# Revit family: PRD_FrankeWS_HndDriers_DryersHandDryer_RODX310
name_source: partatom
category: Specialty Equipment
revit_build: Autodesk Revit 2018 (Build: 20190510_1515(x64)
units: mm (PartAtom-declared; Revit-internal decimal feet)

## family parameters
Cut with Voids When Loaded = No
Host = Face
OmniClass Number = 23.40.20.21.14
OmniClass Title = Hand and Hair Dryers
Part Type = Normal
Room Calculation Point = No
Round Connector Dimension = Use Diameter
Shared = No

## types (1)
- RODX310
    ApparentPower = 2200 VA
    AssetType = Fixed
    BIMObjectName = PRD_AR_HandDriers_DryersHandDryer_RODX310
    BodyEnclosure = Stainless steel
    BodyFinishAndColour = Stainless steel, satin finished
    BodyIngressProtectionMinimum = IPX1
    Category = Pr_40_70_62_37, Hand driers
    Color = Stainless steel
    Default Elevation = 1000 mm  [stored 3.28084 ft]
    Description = Touch free electronic warm air hand dryer for wall mounting, stainless steel, surface satin finished, material thickness 1.2 mm, infrared sensor activity for non-touch operation, sensor range adjustable from 10 to 30 cm, cable and plug not included.
    DurationUnit = year
    ElectricalDeviceNominalPower = 2200 VA
    ElectricalSupplyPowerRating = 2200 W
    ElectricalSupplyRatedOperationalVoltageUe = 230 V a.c.
    Features = Sensor range adjustable from 10 to 30 cm
    Finish = Satin finished
    Form = Touch free electronic warm air hand dryer for wall mounting
    GrossWeight = 7.58 kg
    HandDryerMaterial = PRD_AR_StainlessSteel_SatinFinished
    HasProtectiveEarth = Yes
    IP_Code = IPX1
    IfcExportAs = IfcElectricApplianceType
    IfcExportType = HANDDRYER
    InsulationStandardClass = NotKnown
    LoadClassification = Other
    Manufacturer = KWC Group AG
    ManufacturerName = KWC Group AG
    ManufacturerURL = www.kwc.com
    Material = Stainless steel
    Model = RODX310
    ModelNumber = 2000090055
    ModelReference = RODX310
    NBSDescription = Hand driers
    NBSReference = 45-35-72/334
    Name = DRYERS hand dryer RODX310
    NetWeight = 7.20 kg
    NoiseLevelAt1MMaximum = 68 dB
    NominalCurrent = 0 A
    NominalFrequencyRange = 50
    NominalHeight = 215 mm
    NominalLength = 314 mm  [stored 1.03018 ft]
    NominalVoltage = 230
    NominalWidth = 163 mm  [stored 0.534777 ft]
    NumberOfPoles = 1
    Operation = Automatic. No touch
    PhaseAngle = 0.00°
    PhaseReference = 0
    PowerFactor = 1
    ProductInformation = https://pim.kwc.com
    Size = 314 x 215 x 163 mm
    URL = www.kwc.com
    Uniclass2015Code = Pr_40_70_62_37
    Uniclass2015Title = Hand driers
    Uniclass2015Version = Products v1.5
    UsageCurrent = 0 A
    Version = 1
    Voltage = 230 V
    WarrantyDurationUnit = year

note: [stored X ft] marks values corroborated as IEEE doubles in the binary element streams (Revit-internal decimal feet)

## geometry (parser evidence)
native form markers: Sweep x2
no freeform markers — native parametric forms only
